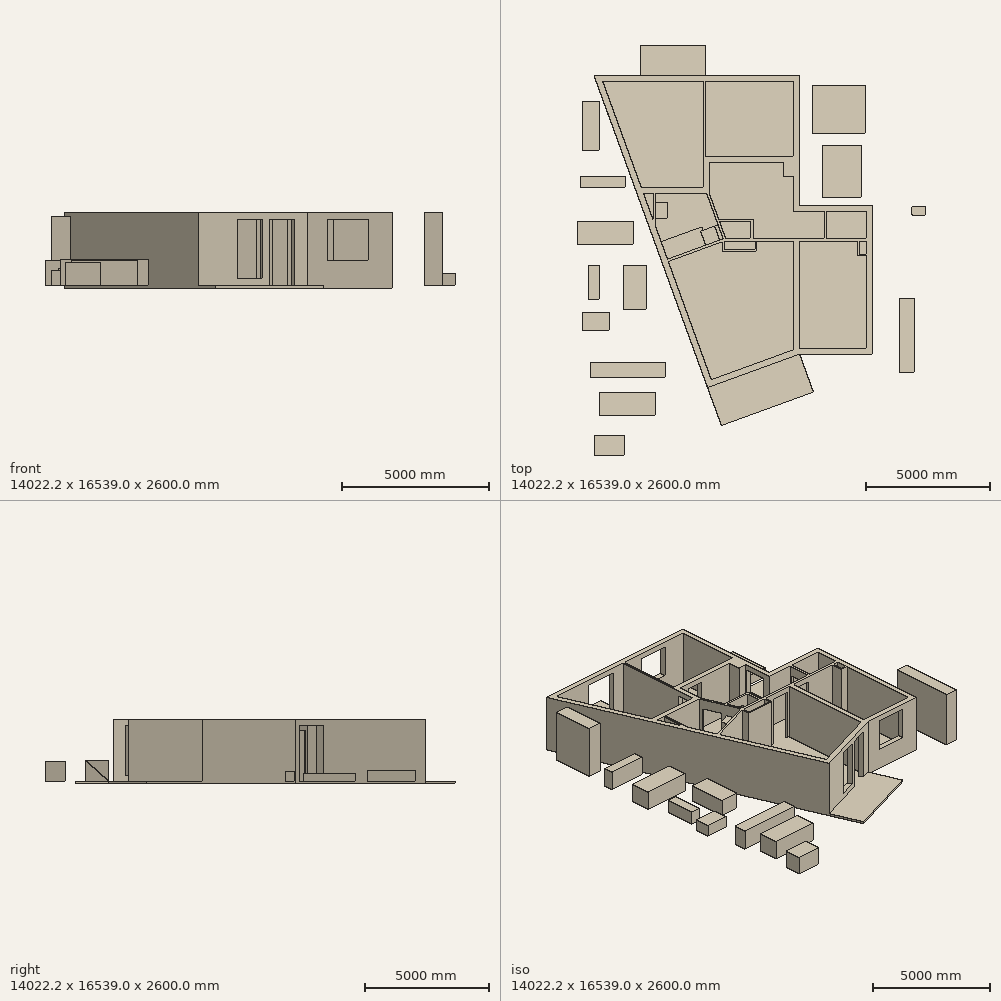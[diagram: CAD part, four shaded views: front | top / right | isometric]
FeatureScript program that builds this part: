
annotation { "Feature Type Name" : "Feature", "Feature Type Description" : "" }
export const myFeature = defineFeature(function(context is Context, id is Id, definition is map)
    precondition{}
    {
        {
            var Q0;
            Q0=qCreatedBy(makeId("Top.planeOp"),FACE);
            var sketch = newSketch(context, id + "F0", { "sketchPlane" : qUnion([Q0])});
            skLineSegment(sketch, "E0", {"start": v(0, 0) * mm, "end": v(8300, 0) * mm});
            skLineSegment(sketch, "E1", {"start": v(8300, 0) * mm, "end": v(8300, -5250) * mm});
            skLineSegment(sketch, "E2", {"start": v(8300, -11255.04) * mm, "end": v(4588.21, -12606.01) * mm});
            skLineSegment(sketch, "E3", {"start": v(4588.21, -12606.01) * mm, "end": v(0, 0) * mm});
            skLineSegment(sketch, "E4.0", {"start": v(357.04, -250) * mm, "end": v(4402.04, -250) * mm});
            skLineSegment(sketch, "E4.1", {"start": v(4737.63, -12285.59) * mm, "end": v(3002.37, -7518) * mm});
            skLineSegment(sketch, "E4.2", {"start": v(8050, -11079.98) * mm, "end": v(4737.63, -12285.59) * mm});
            skLineSegment(sketch, "E4.3", {"start": v(8050, -250) * mm, "end": v(8050, -3260) * mm});
            skLineSegment(sketch, "E5", {"start": v(8050, -3260) * mm, "end": v(4502.04, -3260) * mm});
            skLineSegment(sketch, "E6", {"start": v(4402.04, -3260) * mm, "end": v(4402.04, -4510) * mm});
            skLineSegment(sketch, "E7", {"start": v(4402.04, -4510) * mm, "end": v(1907.55, -4510) * mm});
            skLineSegment(sketch, "E8.0", {"start": v(4545.62, -4760) * mm, "end": v(2498.54, -4760) * mm});
            skLineSegment(sketch, "E8.1", {"start": v(4652.04, -3510) * mm, "end": v(4652.04, -4760) * mm});
            skLineSegment(sketch, "E8.2", {"start": v(8050, -3510) * mm, "end": v(4652.04, -3510) * mm});
            skLineSegment(sketch, "E9", {"start": v(4402.04, -3260) * mm, "end": v(4402.04, -250) * mm});
            skLineSegment(sketch, "E10.0", {"start": v(4502.04, -3260) * mm, "end": v(4502.04, -250) * mm});
            skLineSegment(sketch, "E11", {"start": v(3002.37, -7518) * mm, "end": v(5192.37, -6720.9) * mm});
            skLineSegment(sketch, "E12", {"start": v(4652.04, -4760) * mm, "end": v(5032.4, -5805.04) * mm});
            skLineSegment(sketch, "E13.0", {"start": v(4545.62, -4760) * mm, "end": v(5217.3, -6605.41) * mm});
            skLineSegment(sketch, "E13.1", {"start": v(2968.17, -7424.03) * mm, "end": v(5217.3, -6605.41) * mm});
            skLineSegment(sketch, "E14", {"start": v(2498.54, -4760) * mm, "end": v(2498.54, -6133.74) * mm});
            skLineSegment(sketch, "E15.0", {"start": v(2398.54, -4760) * mm, "end": v(2398.54, -5859) * mm});
            skLineSegment(sketch, "E16", {"start": v(4588.21, -12606.01) * mm, "end": v(5145.7, -14137.71) * mm});
            skLineSegment(sketch, "E17", {"start": v(5145.7, -14137.71) * mm, "end": v(8857.5, -12786.73) * mm});
            skLineSegment(sketch, "E18", {"start": v(8857.5, -12786.73) * mm, "end": v(8300, -11255.04) * mm});
            skLineSegment(sketch, "E19", {"start": v(8300, -5250) * mm, "end": v(11220, -5250) * mm});
            skLineSegment(sketch, "E20", {"start": v(11220, -5250) * mm, "end": v(11220, -11255.04) * mm});
            skLineSegment(sketch, "E21", {"start": v(11220, -11255.04) * mm, "end": v(8300, -11255.04) * mm});
            skLineSegment(sketch, "E22.0", {"start": v(8300, -5500) * mm, "end": v(9300, -5500) * mm});
            skLineSegment(sketch, "E23.0", {"start": v(11000, -5500) * mm, "end": v(11000, -6605.04) * mm});
            skLineSegment(sketch, "E24.0", {"start": v(11000, -11005.04) * mm, "end": v(8300, -11005.04) * mm});
            skLineSegment(sketch, "E25", {"start": v(1900, 0) * mm, "end": v(1900, 1200) * mm});
            skLineSegment(sketch, "E26", {"start": v(1900, 1200) * mm, "end": v(4500, 1200) * mm});
            skLineSegment(sketch, "E27", {"start": v(4500, 1200) * mm, "end": v(4500, 0) * mm});
            skLineSegment(sketch, "E28", {"start": v(11000, -6605.04) * mm, "end": v(9400, -6605.04) * mm});
            skLineSegment(sketch, "E29.0", {"start": v(11000, -6705.04) * mm, "end": v(10710, -6705.04) * mm});
            skLineSegment(sketch, "E30", {"start": v(6323.57, -6605.04) * mm, "end": v(6323.57, -5905.04) * mm});
            skLineSegment(sketch, "E31", {"start": v(6323.57, -5905.04) * mm, "end": v(5068.8, -5905.04) * mm});
            skLineSegment(sketch, "E32.0", {"start": v(6423.57, -5805.04) * mm, "end": v(5032.4, -5805.04) * mm});
            skLineSegment(sketch, "E32.1", {"start": v(6423.57, -6605.04) * mm, "end": v(6423.57, -5805.04) * mm});
            skLineSegment(sketch, "E33", {"start": v(9400, -6605.04) * mm, "end": v(9400, -5500) * mm});
            skLineSegment(sketch, "E34.0", {"start": v(9300, -6605.04) * mm, "end": v(9300, -5500) * mm});
            skLineSegment(sketch, "E35", {"start": v(6512.37, -6705.04) * mm, "end": v(6512.37, -7045.04) * mm});
            skLineSegment(sketch, "E36", {"start": v(6512.37, -7045.04) * mm, "end": v(5252.37, -7045.04) * mm});
            skLineSegment(sketch, "E37", {"start": v(5252.37, -7045.04) * mm, "end": v(5252.37, -6705.04) * mm});
            skLineSegment(sketch, "E38.0", {"start": v(5192.37, -7105.04) * mm, "end": v(5192.37, -6720.9) * mm});
            skLineSegment(sketch, "E38.1", {"start": v(6572.37, -7105.04) * mm, "end": v(5192.37, -7105.04) * mm});
            skLineSegment(sketch, "E38.2", {"start": v(6572.37, -6705.04) * mm, "end": v(6572.37, -7105.04) * mm});
            skLineSegment(sketch, "E39", {"start": v(10650, -6705.04) * mm, "end": v(10650, -7275.04) * mm});
            skLineSegment(sketch, "E40", {"start": v(10650, -7275.04) * mm, "end": v(11000, -7275.04) * mm});
            skLineSegment(sketch, "E41.0", {"start": v(10710, -7215.04) * mm, "end": v(11000, -7215.04) * mm});
            skLineSegment(sketch, "E41.1", {"start": v(10710, -6705.04) * mm, "end": v(10710, -7215.04) * mm});
            skLineSegment(sketch, "E42.trimOffspring", {"start": v(4502.04, -250) * mm, "end": v(8050, -250) * mm});
            skLineSegment(sketch, "E43.trimOffspring", {"start": v(1907.55, -4510) * mm, "end": v(357.04, -250) * mm});
            skLineSegment(sketch, "E44.trimOffspring", {"start": v(2398.54, -5859) * mm, "end": v(1998.54, -4760) * mm});
            skLineSegment(sketch, "E45.trimOffspring", {"start": v(2398.54, -4760) * mm, "end": v(1998.54, -4760) * mm});
            skLineSegment(sketch, "E46.trimOffspring", {"start": v(2968.17, -7424.03) * mm, "end": v(2498.54, -6133.74) * mm});
            skLineSegment(sketch, "E47.trimOffspring", {"start": v(5068.8, -5905.04) * mm, "end": v(5323.57, -6605.04) * mm});
            skLineSegment(sketch, "E48.trimOffspring", {"start": v(6323.57, -6605.04) * mm, "end": v(5323.57, -6605.04) * mm});
            skLineSegment(sketch, "E49.trimOffspring", {"start": v(6512.37, -6705.04) * mm, "end": v(5252.37, -6705.04) * mm});
            skLineSegment(sketch, "E50.trimOffspring", {"start": v(8050, -6705.04) * mm, "end": v(6572.37, -6705.04) * mm});
            skLineSegment(sketch, "E51.trimOffspring", {"start": v(8050, -6705.04) * mm, "end": v(8050, -11079.98) * mm});
            skLineSegment(sketch, "E52.trimOffspring", {"start": v(8050, -6605.04) * mm, "end": v(6423.57, -6605.04) * mm});
            skLineSegment(sketch, "E53.trimOffspring", {"start": v(8300, -5500) * mm, "end": v(8300, -6605.04) * mm});
            skLineSegment(sketch, "E54.trimOffspring", {"start": v(8300, -6705.04) * mm, "end": v(8300, -11005.04) * mm});
            skLineSegment(sketch, "E55.trimOffspring", {"start": v(9300, -6605.04) * mm, "end": v(8300, -6605.04) * mm});
            skLineSegment(sketch, "E56.trimOffspring", {"start": v(9400, -5500) * mm, "end": v(11000, -5500) * mm});
            skLineSegment(sketch, "E57.trimOffspring", {"start": v(10650, -6705.04) * mm, "end": v(8300, -6705.04) * mm});
            skLineSegment(sketch, "E58.trimOffspring", {"start": v(11000, -6705.04) * mm, "end": v(11000, -7215.04) * mm});
            skLineSegment(sketch, "E59.trimOffspring", {"start": v(11000, -7275.04) * mm, "end": v(11000, -11005.04) * mm});
            skLineSegment(sketch, "E60.trimOffspring", {"start": v(8050, -3510) * mm, "end": v(8050, -6605.04) * mm});
            skSolve(sketch);
        }
        {
            var Q0;
            Q0=makeQuery(id+"F0.imprint","IMPRINT",FACE,{"disambiguationData":[TD([[makeQuery(id+"F0.imprint","IMPRINT",EDGE,{"derivedFrom":sQuery(id+"F0.wireOp",EDGE,"E8.1")}),1.0]])]});
            var Q1;
            Q1=makeQuery(id+"F0.imprint","IMPRINT",FACE,{"disambiguationData":[TD([[makeQuery(id+"F0.imprint","IMPRINT",EDGE,{"derivedFrom":sQuery(id+"F0.wireOp",EDGE,"E30")}),1.0]])]});
            var Q2;
            {var subQ2=sQuery(id+"F0.wireOp",EDGE,"E5");Q2=makeQuery(id+"F0.imprint","IMPRINT",FACE,{"disambiguationData":[TD([[makeQuery(id+"F0.imprint","IMPRINT",EDGE,{"derivedFrom":subQ2}),-1.0]])]});}
            var Q3;
            Q3=makeQuery(id+"F0.imprint","IMPRINT",FACE,{"disambiguationData":[TD([[makeQuery(id+"F0.imprint","IMPRINT",EDGE,{"derivedFrom":sQuery(id+"F0.wireOp",EDGE,"E8.0")}),1.0]])]});
            var Q4;
            Q4=makeQuery(id+"F0.imprint","IMPRINT",FACE,{"disambiguationData":[TD([[makeQuery(id+"F0.imprint","IMPRINT",EDGE,{"derivedFrom":sQuery(id+"F0.wireOp",EDGE,"E24.0")}),-1.0]])]});
            var Q5;
            Q5=makeQuery(id+"F0.imprint","IMPRINT",FACE,{"disambiguationData":[TD([[makeQuery(id+"F0.imprint","IMPRINT",EDGE,{"derivedFrom":sQuery(id+"F0.wireOp",EDGE,"E23.0")}),-1.0]])]});
            var Q6;
            Q6=makeQuery(id+"F0.imprint","IMPRINT",FACE,{"disambiguationData":[TD([[makeQuery(id+"F0.imprint","IMPRINT",EDGE,{"derivedFrom":sQuery(id+"F0.wireOp",EDGE,"E4.0")}),-1.0]])]});
            var Q7;
            Q7=makeQuery(id+"F0.imprint","IMPRINT",FACE,{"disambiguationData":[TD([[makeQuery(id+"F0.imprint","IMPRINT",EDGE,{"derivedFrom":sQuery(id+"F0.wireOp",EDGE,"E22.0")}),-1.0]])]});
            var Q8;
            Q8=makeQuery(id+"F0.imprint","IMPRINT",FACE,{"disambiguationData":[TD([[makeQuery(id+"F0.imprint","IMPRINT",EDGE,{"derivedFrom":sQuery(id+"F0.wireOp",EDGE,"E4.1")}),-1.0]])]});
            var Q9;
            Q9=makeQuery(id+"F0.imprint","IMPRINT",FACE,{"disambiguationData":[TD([[makeQuery(id+"F0.imprint","IMPRINT",EDGE,{"derivedFrom":sQuery(id+"F0.wireOp",EDGE,"E2")}),1.0]])]});
            var Q10;
            {var subQ0=sQuery(id+"F0.wireOp",EDGE,"E25");Q10=makeQuery(id+"F0.imprint","IMPRINT",FACE,{"disambiguationData":[TD([[makeQuery(id+"F0.imprint","IMPRINT",EDGE,{"derivedFrom":subQ0}),-1.0]])]});}
            var Q11;
            {var subQ7=sQuery(id+"F0.wireOp",EDGE,"E1");Q11=makeQuery(id+"F0.imprint","IMPRINT",FACE,{"disambiguationData":[TD([[makeQuery(id+"F0.imprint","IMPRINT",EDGE,{"derivedFrom":subQ7}),-1.0]])]});}
            var Q12;
            Q12=makeQuery(id+"F0.imprint","IMPRINT",FACE,{"disambiguationData":[TD([[makeQuery(id+"F0.imprint","IMPRINT",EDGE,{"derivedFrom":sQuery(id+"F0.wireOp",EDGE,"E35")}),-1.0]])]});
            var Q13;
            Q13=makeQuery(id+"F0.imprint","IMPRINT",FACE,{"disambiguationData":[TD([[makeQuery(id+"F0.imprint","IMPRINT",EDGE,{"derivedFrom":sQuery(id+"F0.wireOp",EDGE,"E15.0")}),-1.0]])]});
            var Q14;
            Q14=makeQuery(id+"F0.imprint","IMPRINT",FACE,{"disambiguationData":[TD([[makeQuery(id+"F0.imprint","IMPRINT",EDGE,{"derivedFrom":sQuery(id+"F0.wireOp",EDGE,"E29.0")}),1.0]])]});
            extrude(context, id + "F1", {"entities" : qUnion([Q0, Q1, Q2, Q3, Q4, Q5, Q6, Q7, Q8, Q9, Q10, Q11, Q12, Q13, Q14]), "oppositeDirection" : true, "depth" : 100 * mm});
        }
        {
            var Q0;
            {var subQ4=sQuery(id+"F0.wireOp",EDGE,"E1");Q0=makeQuery(id+"F0.imprint","IMPRINT",FACE,{"disambiguationData":[TD([[makeQuery(id+"F0.imprint","IMPRINT",EDGE,{"derivedFrom":subQ4}),-1.0]])]});}
            extrude(context, id + "F2", {"entities" : qUnion([Q0]), "operationType" : NewBodyOperationType.ADD, "depth" : 2500 * mm});
        }
        {
            var Q0;
            Q0=makeQuery(id+"F2.opExtrude","SWEPT_FACE",FACE,{"disambiguationData":[OSD([sQuery(id+"F0.wireOp",EDGE,"E4.2")])]});
            var sketch = newSketch(context, id + "F3", { "sketchPlane" : qUnion([Q0])});
            skLineSegment(sketch, "E61.bottom", {"start": v(-3475, 0) * mm, "end": v(-2575, 0) * mm});
            skLineSegment(sketch, "E61.top", {"start": v(-3475, 2250) * mm, "end": v(-2575, 2250) * mm});
            skLineSegment(sketch, "E61.left", {"start": v(-3475, 0) * mm, "end": v(-3475, 2250) * mm});
            skLineSegment(sketch, "E61.right", {"start": v(-2575, 0) * mm, "end": v(-2575, 2250) * mm});
            skLineSegment(sketch, "E62.bottom", {"start": v(-2325, 2250) * mm, "end": v(-1425, 2250) * mm});
            skLineSegment(sketch, "E62.top", {"start": v(-2325, 250) * mm, "end": v(-1425, 250) * mm});
            skLineSegment(sketch, "E62.left", {"start": v(-2325, 2250) * mm, "end": v(-2325, 250) * mm});
            skLineSegment(sketch, "E62.right", {"start": v(-1425, 2250) * mm, "end": v(-1425, 250) * mm});
            skSolve(sketch);
        }
        {
            var Q0;
            Q0=makeQuery(id+"F3.imprint","IMPRINT",FACE,{"disambiguationData":[TD([[makeQuery(id+"F3.imprint","IMPRINT",EDGE,{"derivedFrom":sQuery(id+"F3.wireOp",EDGE,"E62.bottom")}),-1.0]])]});
            var Q1;
            Q1=makeQuery(id+"F3.imprint","IMPRINT",FACE,{"disambiguationData":[TD([[makeQuery(id+"F3.imprint","IMPRINT",EDGE,{"derivedFrom":sQuery(id+"F3.wireOp",EDGE,"E61.bottom")}),1.0]])]});
            extrude(context, id + "F4", {"entities" : qUnion([Q0, Q1]), "operationType" : NewBodyOperationType.REMOVE, "endBound" : BoundingType.THROUGH_ALL, "oppositeDirection" : true, "depth" : 25 * mm});
        }
        {
            var Q0;
            Q0=makeQuery(id+"F2.opExtrude","SWEPT_FACE",FACE,{"disambiguationData":[OSD([sQuery(id+"F0.wireOp",EDGE,"E4.0")])]});
            var sketch = newSketch(context, id + "F5", { "sketchPlane" : qUnion([Q0])});
            skLineSegment(sketch, "E63.bottom", {"start": v(3800, 0) * mm, "end": v(2900, 0) * mm});
            skLineSegment(sketch, "E63.top", {"start": v(3800, 2250) * mm, "end": v(2900, 2250) * mm});
            skLineSegment(sketch, "E63.left", {"start": v(3800, 0) * mm, "end": v(3800, 2250) * mm});
            skLineSegment(sketch, "E63.right", {"start": v(2900, 0) * mm, "end": v(2900, 2250) * mm});
            skLineSegment(sketch, "E64.bottom", {"start": v(2900, 2250) * mm, "end": v(2300, 2250) * mm});
            skLineSegment(sketch, "E64.top", {"start": v(2900, 850) * mm, "end": v(2300, 850) * mm});
            skLineSegment(sketch, "E64.left", {"start": v(2900, 2250) * mm, "end": v(2900, 850) * mm});
            skLineSegment(sketch, "E64.right", {"start": v(2300, 2250) * mm, "end": v(2300, 850) * mm});
            skLineSegment(sketch, "E65.0", {"start": v(0, -100) * mm, "end": v(0, 2500) * mm});
            skSolve(sketch);
        }
        {
            var Q0;
            Q0=makeQuery(id+"F5.imprint","IMPRINT",FACE,{"disambiguationData":[TD([[makeQuery(id+"F5.imprint","IMPRINT",EDGE,{"derivedFrom":sQuery(id+"F5.wireOp",EDGE,"E64.bottom")}),1.0]])]});
            var Q1;
            Q1=makeQuery(id+"F5.imprint","IMPRINT",FACE,{"disambiguationData":[TD([[makeQuery(id+"F5.imprint","IMPRINT",EDGE,{"derivedFrom":sQuery(id+"F5.wireOp",EDGE,"E63.bottom")}),1.0]])]});
            extrude(context, id + "F6", {"entities" : qUnion([Q0, Q1]), "operationType" : NewBodyOperationType.REMOVE, "endBound" : BoundingType.THROUGH_ALL, "oppositeDirection" : true, "depth" : 25 * mm});
        }
        {
            var Q0;
            Q0=makeQuery(id+"F2.opExtrude","SWEPT_FACE",FACE,{"disambiguationData":[OSD([sQuery(id+"F0.wireOp",EDGE,"E42.trimOffspring")])]});
            var sketch = newSketch(context, id + "F7", { "sketchPlane" : qUnion([Q0])});
            skLineSegment(sketch, "E66.bottom", {"start": v(5550, 2250) * mm, "end": v(6950, 2250) * mm});
            skLineSegment(sketch, "E66.top", {"start": v(5550, 850) * mm, "end": v(6950, 850) * mm});
            skLineSegment(sketch, "E66.left", {"start": v(5550, 2250) * mm, "end": v(5550, 850) * mm});
            skLineSegment(sketch, "E66.right", {"start": v(6950, 2250) * mm, "end": v(6950, 850) * mm});
            skLineSegment(sketch, "E67.0", {"start": v(0, -100) * mm, "end": v(0, 2500) * mm});
            skSolve(sketch);
        }
        {
            var Q0;
            Q0=makeQuery(id+"F7.imprint","IMPRINT",FACE,{"disambiguationData":[TD([[makeQuery(id+"F7.imprint","IMPRINT",EDGE,{"derivedFrom":sQuery(id+"F7.wireOp",EDGE,"E66.bottom")}),-1.0]])]});
            extrude(context, id + "F8", {"entities" : qUnion([Q0]), "operationType" : NewBodyOperationType.REMOVE, "endBound" : BoundingType.THROUGH_ALL, "oppositeDirection" : true, "depth" : 25 * mm});
        }
        {
            var Q0;
            Q0=makeQuery(id+"F2.opExtrude","SWEPT_FACE",FACE,{"disambiguationData":[OSD([sQuery(id+"F0.wireOp",EDGE,"E24.0")])]});
            var sketch = newSketch(context, id + "F9", { "sketchPlane" : qUnion([Q0])});
            skLineSegment(sketch, "E68.bottom", {"start": v(-10400, 850) * mm, "end": v(-9000, 850) * mm});
            skLineSegment(sketch, "E68.top", {"start": v(-10400, 2250) * mm, "end": v(-9000, 2250) * mm});
            skLineSegment(sketch, "E68.left", {"start": v(-10400, 850) * mm, "end": v(-10400, 2250) * mm});
            skLineSegment(sketch, "E68.right", {"start": v(-9000, 850) * mm, "end": v(-9000, 2250) * mm});
            skSolve(sketch);
        }
        {
            var Q0;
            Q0=makeQuery(id+"F9.imprint","IMPRINT",FACE,{"disambiguationData":[TD([[makeQuery(id+"F9.imprint","IMPRINT",EDGE,{"derivedFrom":sQuery(id+"F9.wireOp",EDGE,"E68.bottom")}),1.0]])]});
            extrude(context, id + "F10", {"entities" : qUnion([Q0]), "operationType" : NewBodyOperationType.REMOVE, "endBound" : BoundingType.THROUGH_ALL, "oppositeDirection" : true, "depth" : 25 * mm});
        }
        {
            var Q0;
            Q0=makeQuery(id+"F2.opExtrude","SWEPT_FACE",FACE,{"disambiguationData":[OSD([sQuery(id+"F0.wireOp",EDGE,"E34.0")])]});
            var sketch = newSketch(context, id + "F11", { "sketchPlane" : qUnion([Q0])});
            skLineSegment(sketch, "E69", {"start": v(6052.52, 0) * mm, "end": v(6502.52, 0) * mm});
            skLineSegment(sketch, "E70", {"start": v(6502.52, 0) * mm, "end": v(6502.52, 2050) * mm});
            skLineSegment(sketch, "E71", {"start": v(6502.52, 2050) * mm, "end": v(5602.52, 2050) * mm});
            skLineSegment(sketch, "E72", {"start": v(5602.52, 2050) * mm, "end": v(5602.52, 0) * mm});
            skLineSegment(sketch, "E73", {"start": v(5602.52, 0) * mm, "end": v(6052.52, 0) * mm});
            skSolve(sketch);
        }
        {
            var Q0;
            Q0=makeQuery(id+"F11.imprint","IMPRINT",FACE,{"disambiguationData":[TD([[makeQuery(id+"F11.imprint","IMPRINT",EDGE,{"derivedFrom":sQuery(id+"F11.wireOp",EDGE,"E69")}),-1.0]])]});
            extrude(context, id + "F12", {"entities" : qUnion([Q0]), "operationType" : NewBodyOperationType.REMOVE, "endBound" : BoundingType.UP_TO_NEXT, "oppositeDirection" : true, "depth" : 25 * mm});
        }
        {
            var Q0;
            Q0=makeQuery(id+"F2.opExtrude","SWEPT_FACE",FACE,{"disambiguationData":[OSD([sQuery(id+"F0.wireOp",EDGE,"E55.trimOffspring")])]});
            var sketch = newSketch(context, id + "F13", { "sketchPlane" : qUnion([Q0])});
            skLineSegment(sketch, "E74", {"start": v(-8800, 0) * mm, "end": v(-8400, 0) * mm});
            skLineSegment(sketch, "E75", {"start": v(-8400, 0) * mm, "end": v(-8400, 2250) * mm});
            skLineSegment(sketch, "E76", {"start": v(-8400, 2250) * mm, "end": v(-9200, 2250) * mm});
            skLineSegment(sketch, "E77", {"start": v(-9200, 2250) * mm, "end": v(-9200, 0) * mm});
            skLineSegment(sketch, "E78", {"start": v(-9200, 0) * mm, "end": v(-8800, 0) * mm});
            skSolve(sketch);
        }
        {
            var Q0;
            Q0=makeQuery(id+"F13.imprint","IMPRINT",FACE,{"disambiguationData":[TD([[makeQuery(id+"F13.imprint","IMPRINT",EDGE,{"derivedFrom":sQuery(id+"F13.wireOp",EDGE,"E74")}),1.0]])]});
            extrude(context, id + "F14", {"entities" : qUnion([Q0]), "operationType" : NewBodyOperationType.REMOVE, "endBound" : BoundingType.UP_TO_NEXT, "oppositeDirection" : true, "depth" : 25 * mm});
        }
        {
            var Q0;
            Q0=makeQuery(id+"F2.opExtrude","SWEPT_FACE",FACE,{"disambiguationData":[OSD([sQuery(id+"F0.wireOp",EDGE,"E53.trimOffspring")])]});
            var sketch = newSketch(context, id + "F15", { "sketchPlane" : qUnion([Q0])});
            skLineSegment(sketch, "E79.bottom", {"start": v(-6605.04, 0) * mm, "end": v(-5500, 0) * mm});
            skLineSegment(sketch, "E79.top", {"start": v(-6605.04, 2500) * mm, "end": v(-5500, 2500) * mm});
            skLineSegment(sketch, "E79.left", {"start": v(-6605.04, 0) * mm, "end": v(-6605.04, 2500) * mm});
            skLineSegment(sketch, "E79.right", {"start": v(-5500, 0) * mm, "end": v(-5500, 2500) * mm});
            skSolve(sketch);
        }
        {
            var Q0;
            Q0 = qSketchRegion(id + "F15", true);
            extrude(context, id + "F16", {"entities" : qUnion([Q0]), "operationType" : NewBodyOperationType.REMOVE, "endBound" : BoundingType.UP_TO_NEXT, "oppositeDirection" : true, "depth" : 25 * mm});
        }
        {
            var Q0;
            Q0=makeQuery(id+"F2.opExtrude","SWEPT_FACE",FACE,{"disambiguationData":[OSD([sQuery(id+"F0.wireOp",EDGE,"E31")])]});
            var sketch = newSketch(context, id + "F17", { "sketchPlane" : qUnion([Q0])});
            skLineSegment(sketch, "E80", {"start": v(5696.19, 0) * mm, "end": v(6046.19, 0) * mm});
            skLineSegment(sketch, "E81", {"start": v(6046.19, 0) * mm, "end": v(6046.19, 2050) * mm});
            skLineSegment(sketch, "E82", {"start": v(6046.19, 2050) * mm, "end": v(5346.19, 2050) * mm});
            skLineSegment(sketch, "E83", {"start": v(5346.19, 2050) * mm, "end": v(5346.19, 0) * mm});
            skLineSegment(sketch, "E84", {"start": v(5346.19, 0) * mm, "end": v(5696.19, 0) * mm});
            skSolve(sketch);
        }
        {
            var Q0;
            Q0 = qSketchRegion(id + "F17", true);
            extrude(context, id + "F18", {"entities" : qUnion([Q0]), "operationType" : NewBodyOperationType.REMOVE, "endBound" : BoundingType.UP_TO_NEXT, "oppositeDirection" : true, "depth" : 25 * mm});
        }
        {
            var Q0;
            Q0=makeQuery(id+"F2.opExtrude","SWEPT_FACE",FACE,{"disambiguationData":[OSD([sQuery(id+"F0.wireOp",EDGE,"E60.trimOffspring")])]});
            var sketch = newSketch(context, id + "F19", { "sketchPlane" : qUnion([Q0])});
            skLineSegment(sketch, "E85.bottom", {"start": v(5110, 0) * mm, "end": v(4110, 0) * mm});
            skLineSegment(sketch, "E85.top", {"start": v(5110, 2250) * mm, "end": v(4110, 2250) * mm});
            skLineSegment(sketch, "E85.left", {"start": v(5110, 0) * mm, "end": v(5110, 2250) * mm});
            skLineSegment(sketch, "E85.right", {"start": v(4110, 0) * mm, "end": v(4110, 2250) * mm});
            skSolve(sketch);
        }
        {
            var Q0;
            Q0 = qSketchRegion(id + "F19", true);
            extrude(context, id + "F20", {"entities" : qUnion([Q0]), "operationType" : NewBodyOperationType.REMOVE, "endBound" : BoundingType.UP_TO_NEXT, "oppositeDirection" : true, "depth" : 25 * mm});
        }
        {
            var Q0;
            Q0=makeQuery(id+"F2.opExtrude","SWEPT_FACE",FACE,{"disambiguationData":[OSD([sQuery(id+"F0.wireOp",EDGE,"E8.2")])]});
            var sketch = newSketch(context, id + "F21", { "sketchPlane" : qUnion([Q0])});
            skLineSegment(sketch, "E86.bottom", {"start": v(5132.04, 0) * mm, "end": v(5932.04, 0) * mm});
            skLineSegment(sketch, "E86.top", {"start": v(5132.04, 2250) * mm, "end": v(5932.04, 2250) * mm});
            skLineSegment(sketch, "E86.left", {"start": v(5132.04, 0) * mm, "end": v(5132.04, 2250) * mm});
            skLineSegment(sketch, "E86.right", {"start": v(5932.04, 0) * mm, "end": v(5932.04, 2250) * mm});
            skSolve(sketch);
        }
        {
            var Q0;
            Q0 = qSketchRegion(id + "F21", true);
            extrude(context, id + "F22", {"entities" : qUnion([Q0]), "operationType" : NewBodyOperationType.REMOVE, "endBound" : BoundingType.UP_TO_NEXT, "oppositeDirection" : true, "depth" : 25 * mm});
        }
        {
            var Q0;
            Q0=makeQuery(id+"F2.opExtrude","SWEPT_FACE",FACE,{"disambiguationData":[OSD([sQuery(id+"F0.wireOp",EDGE,"E8.1")])]});
            var sketch = newSketch(context, id + "F23", { "sketchPlane" : qUnion([Q0])});
            skLineSegment(sketch, "E87.0", {"start": v(-4510, 2500) * mm, "end": v(-4510, 0) * mm});
            skLineSegment(sketch, "E88.bottom", {"start": v(-4410, 0) * mm, "end": v(-3610, 0) * mm});
            skLineSegment(sketch, "E88.top", {"start": v(-4410, 2250) * mm, "end": v(-3610, 2250) * mm});
            skLineSegment(sketch, "E88.left", {"start": v(-4410, 0) * mm, "end": v(-4410, 2250) * mm});
            skLineSegment(sketch, "E88.right", {"start": v(-3610, 0) * mm, "end": v(-3610, 2250) * mm});
            skSolve(sketch);
        }
        {
            var Q0;
            Q0 = qSketchRegion(id + "F23", true);
            extrude(context, id + "F24", {"entities" : qUnion([Q0]), "operationType" : NewBodyOperationType.REMOVE, "endBound" : BoundingType.UP_TO_NEXT, "oppositeDirection" : true, "depth" : 25 * mm});
        }
        {
            var Q0;
            Q0=makeQuery(id+"F2.opExtrude","SWEPT_FACE",FACE,{"disambiguationData":[OSD([sQuery(id+"F0.wireOp",EDGE,"E50.trimOffspring")])]});
            var sketch = newSketch(context, id + "F25", { "sketchPlane" : qUnion([Q0])});
            skLineSegment(sketch, "E89.bottom", {"start": v(7910, 0) * mm, "end": v(7110, 0) * mm});
            skLineSegment(sketch, "E89.top", {"start": v(7910, 2250) * mm, "end": v(7110, 2250) * mm});
            skLineSegment(sketch, "E89.left", {"start": v(7910, 0) * mm, "end": v(7910, 2250) * mm});
            skLineSegment(sketch, "E89.right", {"start": v(7110, 0) * mm, "end": v(7110, 2250) * mm});
            skSolve(sketch);
        }
        {
            var Q0;
            Q0 = qSketchRegion(id + "F25", true);
            extrude(context, id + "F26", {"entities" : qUnion([Q0]), "operationType" : NewBodyOperationType.REMOVE, "endBound" : BoundingType.UP_TO_NEXT, "oppositeDirection" : true, "depth" : 25 * mm});
        }
        {
            var Q0;
            Q0=makeQuery(id+"F2.opExtrude","SWEPT_FACE",FACE,{"disambiguationData":[OSD([sQuery(id+"F0.wireOp",EDGE,"E12")])]});
            var sketch = newSketch(context, id + "F27", { "sketchPlane" : qUnion([Q0])});
            skLineSegment(sketch, "E90", {"start": v(-6620.08, 0) * mm, "end": v(-6170.08, 0) * mm});
            skLineSegment(sketch, "E91", {"start": v(-6170.08, 0) * mm, "end": v(-6170.08, 2050) * mm});
            skLineSegment(sketch, "E92", {"start": v(-6170.08, 2050) * mm, "end": v(-7070.08, 2050) * mm});
            skLineSegment(sketch, "E93", {"start": v(-7070.08, 2050) * mm, "end": v(-7070.08, 0) * mm});
            skLineSegment(sketch, "E94", {"start": v(-7070.08, 0) * mm, "end": v(-6620.08, 0) * mm});
            skSolve(sketch);
        }
        {
            var Q0;
            Q0 = qSketchRegion(id + "F27", true);
            extrude(context, id + "F28", {"entities" : qUnion([Q0]), "operationType" : NewBodyOperationType.REMOVE, "endBound" : BoundingType.UP_TO_NEXT, "oppositeDirection" : true, "depth" : 25 * mm});
        }
        {
            var Q0;
            {var subQ0=sQuery(id+"F0.wireOp",EDGE,"E27");var subQ1=sQuery(id+"F0.wireOp",EDGE,"E26");var subQ2=sQuery(id+"F0.wireOp",EDGE,"E25");var subQ3=sQuery(id+"F0.wireOp",EDGE,"E21");var subQ4=sQuery(id+"F0.wireOp",EDGE,"E18");var subQ5=sQuery(id+"F0.wireOp",EDGE,"E17");var subQ6=sQuery(id+"F0.wireOp",EDGE,"E16");var subQ7=sQuery(id+"F0.wireOp",EDGE,"E3");var subQ8=sQuery(id+"F0.wireOp",EDGE,"E1");var subQ9=sQuery(id+"F0.wireOp",EDGE,"E0");var subQ10=makeQuery(id+"F1.opExtrude","CAP_FACE",FACE,{"disambiguationData":[OSD([subQ9,subQ8,subQ7,subQ6,subQ5,subQ4,sQuery(id+"F0.wireOp",EDGE,"E19"),sQuery(id+"F0.wireOp",EDGE,"E20"),subQ3,subQ2,subQ1,subQ0])],"isStart":true});Q0=makeQuery(id+"F28.boolean.opBoolean","MERGE",FACE,{"derivedFrom":[makeQuery(id+"F2.boolean.opBoolean","SPLIT",FACE,{"disambiguationData":[TD([makeQuery(id+"F2.opExtrude","SWEPT_FACE",FACE,{"disambiguationData":[OSD([sQuery(id+"F0.wireOp",EDGE,"E8.0")])]})])],"derivedFrom":subQ10}),makeQuery(id+"F26.boolean.opBoolean","MERGE",FACE,{"derivedFrom":[makeQuery(id+"F4.boolean.opBoolean","MERGE",FACE,{"derivedFrom":[makeQuery(id+"F2.boolean.opBoolean","SPLIT",FACE,{"disambiguationData":[TD([makeQuery(id+"F1.opExtrude","SWEPT_FACE",FACE,{"disambiguationData":[OSD([subQ5])]})])],"derivedFrom":subQ10}),makeQuery(id+"F2.boolean.opBoolean","SPLIT",FACE,{"disambiguationData":[TD([makeQuery(id+"F2.opExtrude","SWEPT_FACE",FACE,{"disambiguationData":[OSD([sQuery(id+"F0.wireOp",EDGE,"E4.1")])]})])],"derivedFrom":subQ10}),makeQuery(id+"F4.opExtrude","SWEPT_FACE",FACE,{"disambiguationData":[OSD([sQuery(id+"F3.wireOp",EDGE,"E61.bottom")])]})]}),makeQuery(id+"F24.boolean.opBoolean","MERGE",FACE,{"derivedFrom":[makeQuery(id+"F6.boolean.opBoolean","MERGE",FACE,{"derivedFrom":[makeQuery(id+"F2.boolean.opBoolean","SPLIT",FACE,{"disambiguationData":[TD([makeQuery(id+"F1.opExtrude","SWEPT_FACE",FACE,{"disambiguationData":[OSD([subQ2])]})])],"derivedFrom":subQ10}),makeQuery(id+"F2.boolean.opBoolean","SPLIT",FACE,{"disambiguationData":[TD([makeQuery(id+"F2.opExtrude","SWEPT_FACE",FACE,{"disambiguationData":[OSD([sQuery(id+"F0.wireOp",EDGE,"E4.0")])]})])],"derivedFrom":subQ10}),makeQuery(id+"F6.opExtrude","SWEPT_FACE",FACE,{"disambiguationData":[OSD([sQuery(id+"F5.wireOp",EDGE,"E63.bottom")])]})]}),makeQuery(id+"F22.boolean.opBoolean","MERGE",FACE,{"derivedFrom":[makeQuery(id+"F2.boolean.opBoolean","SPLIT",FACE,{"disambiguationData":[TD([makeQuery(id+"F2.opExtrude","SWEPT_FACE",FACE,{"disambiguationData":[OSD([sQuery(id+"F0.wireOp",EDGE,"E4.3")])]})])],"derivedFrom":subQ10}),makeQuery(id+"F20.boolean.opBoolean","MERGE",FACE,{"derivedFrom":[makeQuery(id+"F18.boolean.opBoolean","MERGE",FACE,{"derivedFrom":[makeQuery(id+"F2.boolean.opBoolean","SPLIT",FACE,{"disambiguationData":[TD([makeQuery(id+"F2.opExtrude","SWEPT_FACE",FACE,{"disambiguationData":[OSD([sQuery(id+"F0.wireOp",EDGE,"E30")])]})])],"derivedFrom":subQ10}),makeQuery(id+"F16.boolean.opBoolean","MERGE",FACE,{"derivedFrom":[makeQuery(id+"F2.boolean.opBoolean","SPLIT",FACE,{"disambiguationData":[TD([makeQuery(id+"F2.opExtrude","SWEPT_FACE",FACE,{"disambiguationData":[OSD([sQuery(id+"F0.wireOp",EDGE,"E8.1")])]})])],"derivedFrom":subQ10}),makeQuery(id+"F14.boolean.opBoolean","MERGE",FACE,{"derivedFrom":[makeQuery(id+"F2.boolean.opBoolean","SPLIT",FACE,{"disambiguationData":[TD([makeQuery(id+"F2.opExtrude","SWEPT_FACE",FACE,{"disambiguationData":[OSD([sQuery(id+"F0.wireOp",EDGE,"E24.0")])]})])],"derivedFrom":subQ10}),makeQuery(id+"F12.boolean.opBoolean","MERGE",FACE,{"derivedFrom":[makeQuery(id+"F2.boolean.opBoolean","SPLIT",FACE,{"disambiguationData":[TD([makeQuery(id+"F2.opExtrude","SWEPT_FACE",FACE,{"disambiguationData":[OSD([sQuery(id+"F0.wireOp",EDGE,"E22.0")])]})])],"derivedFrom":subQ10}),makeQuery(id+"F2.boolean.opBoolean","SPLIT",FACE,{"disambiguationData":[TD([makeQuery(id+"F2.opExtrude","SWEPT_FACE",FACE,{"disambiguationData":[OSD([sQuery(id+"F0.wireOp",EDGE,"E23.0")])]})])],"derivedFrom":subQ10}),makeQuery(id+"F12.opExtrude","SWEPT_FACE",FACE,{"disambiguationData":[OSD([sQuery(id+"F11.wireOp",EDGE,"E69"),sQuery(id+"F11.wireOp",EDGE,"E73")])]})]}),makeQuery(id+"F14.opExtrude","SWEPT_FACE",FACE,{"disambiguationData":[OSD([sQuery(id+"F13.wireOp",EDGE,"E74"),sQuery(id+"F13.wireOp",EDGE,"E78")])]})]}),makeQuery(id+"F16.opExtrude","SWEPT_FACE",FACE,{"disambiguationData":[OSD([sQuery(id+"F15.wireOp",EDGE,"E79.bottom")])]})]}),makeQuery(id+"F18.opExtrude","SWEPT_FACE",FACE,{"disambiguationData":[OSD([sQuery(id+"F17.wireOp",EDGE,"E80"),sQuery(id+"F17.wireOp",EDGE,"E84")])]})]}),makeQuery(id+"F20.opExtrude","SWEPT_FACE",FACE,{"disambiguationData":[OSD([sQuery(id+"F19.wireOp",EDGE,"E85.bottom")])]})]}),makeQuery(id+"F22.opExtrude","SWEPT_FACE",FACE,{"disambiguationData":[OSD([sQuery(id+"F21.wireOp",EDGE,"E86.bottom")])]})]}),makeQuery(id+"F24.opExtrude","SWEPT_FACE",FACE,{"disambiguationData":[OSD([sQuery(id+"F23.wireOp",EDGE,"E88.bottom")])]})]}),makeQuery(id+"F26.opExtrude","SWEPT_FACE",FACE,{"disambiguationData":[OSD([sQuery(id+"F25.wireOp",EDGE,"E89.bottom")])]})]}),makeQuery(id+"F28.opExtrude","SWEPT_FACE",FACE,{"disambiguationData":[OSD([sQuery(id+"F27.wireOp",EDGE,"E90"),sQuery(id+"F27.wireOp",EDGE,"E94")])]})]});}
            var sketch = newSketch(context, id + "F29", { "sketchPlane" : qUnion([Q0])});
            skPoint(sketch, "E95.0", {"position": v(3800, -250) * mm});
            skArc(sketch, "E96", {"start": v(2900, -250) * mm, "mid": v(3163.6, -886.4) * mm, "end": v(3800, -1150) * mm});
            skLineSegment(sketch, "E97", {"start": v(3800, -1150) * mm, "end": v(3800, -250) * mm});
            skArc(sketch, "E98", {"start": v(4402.04, -3610) * mm, "mid": v(3836.35, -3844.31) * mm, "end": v(3602.04, -4410) * mm});
            skLineSegment(sketch, "E99", {"start": v(3602.04, -4410) * mm, "end": v(4402.04, -4410) * mm});
            skArc(sketch, "E100", {"start": v(5932.04, -3260) * mm, "mid": v(5697.72, -2694.31) * mm, "end": v(5132.04, -2460) * mm});
            skLineSegment(sketch, "E101", {"start": v(5132.04, -2460) * mm, "end": v(5132.04, -3260) * mm});
            skArc(sketch, "E102", {"start": v(4902.16, -5739.58) * mm, "mid": v(4213.98, -5709.53) * mm, "end": v(3748.62, -5201.68) * mm});
            skLineSegment(sketch, "E103", {"start": v(4594.34, -4893.86) * mm, "end": v(3748.62, -5201.68) * mm});
            skArc(sketch, "E104", {"start": v(5346.19, -5805.04) * mm, "mid": v(5551.21, -5310.06) * mm, "end": v(6046.19, -5105.04) * mm});
            skArc(sketch, "E105", {"start": v(8050, -5110) * mm, "mid": v(7342.9, -4817.1) * mm, "end": v(7050, -4110) * mm});
            skArc(sketch, "E106", {"start": v(9200, -6705.04) * mm, "mid": v(8965.69, -7270.72) * mm, "end": v(8400, -7505.04) * mm});
            skArc(sketch, "E107", {"start": v(7110, -6705.04) * mm, "mid": v(7344.31, -7270.72) * mm, "end": v(7910, -7505.04) * mm});
            skArc(sketch, "E108", {"start": v(6922.42, -11490.39) * mm, "mid": v(6952.46, -10802.22) * mm, "end": v(7460.32, -10336.85) * mm});
            skLineSegment(sketch, "E109", {"start": v(7768.14, -11182.57) * mm, "end": v(7460.32, -10336.85) * mm});
            skLineSegment(sketch, "E110", {"start": v(8400, -7505.04) * mm, "end": v(8400, -6705.04) * mm});
            skLineSegment(sketch, "E111", {"start": v(7910, -6705.04) * mm, "end": v(7910, -7505.04) * mm});
            skLineSegment(sketch, "E112", {"start": v(7050, -4110) * mm, "end": v(8050, -4110) * mm});
            skLineSegment(sketch, "E113", {"start": v(6046.19, -5105.04) * mm, "end": v(6046.19, -5805.04) * mm});
            skArc(sketch, "E114", {"start": v(9400, -6502.52) * mm, "mid": v(10036.4, -6238.91) * mm, "end": v(10300, -5602.52) * mm});
            skLineSegment(sketch, "E115", {"start": v(9400, -5602.52) * mm, "end": v(10300, -5602.52) * mm});
            skSolve(sketch);
        }
        {
            var Q0;
            {var subQ0=sQuery(id+"F0.wireOp",EDGE,"E27");var subQ1=sQuery(id+"F0.wireOp",EDGE,"E26");var subQ2=sQuery(id+"F0.wireOp",EDGE,"E25");var subQ3=sQuery(id+"F0.wireOp",EDGE,"E21");var subQ4=sQuery(id+"F0.wireOp",EDGE,"E18");var subQ5=sQuery(id+"F0.wireOp",EDGE,"E17");var subQ6=sQuery(id+"F0.wireOp",EDGE,"E16");var subQ7=sQuery(id+"F0.wireOp",EDGE,"E3");var subQ8=sQuery(id+"F0.wireOp",EDGE,"E1");var subQ9=sQuery(id+"F0.wireOp",EDGE,"E0");var subQ10=makeQuery(id+"F1.opExtrude","CAP_FACE",FACE,{"disambiguationData":[OSD([subQ9,subQ8,subQ7,subQ6,subQ5,subQ4,sQuery(id+"F0.wireOp",EDGE,"E19"),sQuery(id+"F0.wireOp",EDGE,"E20"),subQ3,subQ2,subQ1,subQ0])],"isStart":true});Q0=makeQuery(id+"F28.boolean.opBoolean","MERGE",FACE,{"derivedFrom":[makeQuery(id+"F2.boolean.opBoolean","SPLIT",FACE,{"disambiguationData":[TD([makeQuery(id+"F2.opExtrude","SWEPT_FACE",FACE,{"disambiguationData":[OSD([sQuery(id+"F0.wireOp",EDGE,"E8.0")])]})])],"derivedFrom":subQ10}),makeQuery(id+"F26.boolean.opBoolean","MERGE",FACE,{"derivedFrom":[makeQuery(id+"F4.boolean.opBoolean","MERGE",FACE,{"derivedFrom":[makeQuery(id+"F2.boolean.opBoolean","SPLIT",FACE,{"disambiguationData":[TD([makeQuery(id+"F1.opExtrude","SWEPT_FACE",FACE,{"disambiguationData":[OSD([subQ5])]})])],"derivedFrom":subQ10}),makeQuery(id+"F2.boolean.opBoolean","SPLIT",FACE,{"disambiguationData":[TD([makeQuery(id+"F2.opExtrude","SWEPT_FACE",FACE,{"disambiguationData":[OSD([sQuery(id+"F0.wireOp",EDGE,"E4.1")])]})])],"derivedFrom":subQ10}),makeQuery(id+"F4.opExtrude","SWEPT_FACE",FACE,{"disambiguationData":[OSD([sQuery(id+"F3.wireOp",EDGE,"E61.bottom")])]})]}),makeQuery(id+"F24.boolean.opBoolean","MERGE",FACE,{"derivedFrom":[makeQuery(id+"F6.boolean.opBoolean","MERGE",FACE,{"derivedFrom":[makeQuery(id+"F2.boolean.opBoolean","SPLIT",FACE,{"disambiguationData":[TD([makeQuery(id+"F1.opExtrude","SWEPT_FACE",FACE,{"disambiguationData":[OSD([subQ2])]})])],"derivedFrom":subQ10}),makeQuery(id+"F2.boolean.opBoolean","SPLIT",FACE,{"disambiguationData":[TD([makeQuery(id+"F2.opExtrude","SWEPT_FACE",FACE,{"disambiguationData":[OSD([sQuery(id+"F0.wireOp",EDGE,"E4.0")])]})])],"derivedFrom":subQ10}),makeQuery(id+"F6.opExtrude","SWEPT_FACE",FACE,{"disambiguationData":[OSD([sQuery(id+"F5.wireOp",EDGE,"E63.bottom")])]})]}),makeQuery(id+"F22.boolean.opBoolean","MERGE",FACE,{"derivedFrom":[makeQuery(id+"F2.boolean.opBoolean","SPLIT",FACE,{"disambiguationData":[TD([makeQuery(id+"F2.opExtrude","SWEPT_FACE",FACE,{"disambiguationData":[OSD([sQuery(id+"F0.wireOp",EDGE,"E4.3")])]})])],"derivedFrom":subQ10}),makeQuery(id+"F20.boolean.opBoolean","MERGE",FACE,{"derivedFrom":[makeQuery(id+"F18.boolean.opBoolean","MERGE",FACE,{"derivedFrom":[makeQuery(id+"F2.boolean.opBoolean","SPLIT",FACE,{"disambiguationData":[TD([makeQuery(id+"F2.opExtrude","SWEPT_FACE",FACE,{"disambiguationData":[OSD([sQuery(id+"F0.wireOp",EDGE,"E30")])]})])],"derivedFrom":subQ10}),makeQuery(id+"F16.boolean.opBoolean","MERGE",FACE,{"derivedFrom":[makeQuery(id+"F2.boolean.opBoolean","SPLIT",FACE,{"disambiguationData":[TD([makeQuery(id+"F2.opExtrude","SWEPT_FACE",FACE,{"disambiguationData":[OSD([sQuery(id+"F0.wireOp",EDGE,"E8.1")])]})])],"derivedFrom":subQ10}),makeQuery(id+"F14.boolean.opBoolean","MERGE",FACE,{"derivedFrom":[makeQuery(id+"F2.boolean.opBoolean","SPLIT",FACE,{"disambiguationData":[TD([makeQuery(id+"F2.opExtrude","SWEPT_FACE",FACE,{"disambiguationData":[OSD([sQuery(id+"F0.wireOp",EDGE,"E24.0")])]})])],"derivedFrom":subQ10}),makeQuery(id+"F12.boolean.opBoolean","MERGE",FACE,{"derivedFrom":[makeQuery(id+"F2.boolean.opBoolean","SPLIT",FACE,{"disambiguationData":[TD([makeQuery(id+"F2.opExtrude","SWEPT_FACE",FACE,{"disambiguationData":[OSD([sQuery(id+"F0.wireOp",EDGE,"E22.0")])]})])],"derivedFrom":subQ10}),makeQuery(id+"F2.boolean.opBoolean","SPLIT",FACE,{"disambiguationData":[TD([makeQuery(id+"F2.opExtrude","SWEPT_FACE",FACE,{"disambiguationData":[OSD([sQuery(id+"F0.wireOp",EDGE,"E23.0")])]})])],"derivedFrom":subQ10}),makeQuery(id+"F12.opExtrude","SWEPT_FACE",FACE,{"disambiguationData":[OSD([sQuery(id+"F11.wireOp",EDGE,"E69"),sQuery(id+"F11.wireOp",EDGE,"E73")])]})]}),makeQuery(id+"F14.opExtrude","SWEPT_FACE",FACE,{"disambiguationData":[OSD([sQuery(id+"F13.wireOp",EDGE,"E74"),sQuery(id+"F13.wireOp",EDGE,"E78")])]})]}),makeQuery(id+"F16.opExtrude","SWEPT_FACE",FACE,{"disambiguationData":[OSD([sQuery(id+"F15.wireOp",EDGE,"E79.bottom")])]})]}),makeQuery(id+"F18.opExtrude","SWEPT_FACE",FACE,{"disambiguationData":[OSD([sQuery(id+"F17.wireOp",EDGE,"E80"),sQuery(id+"F17.wireOp",EDGE,"E84")])]})]}),makeQuery(id+"F20.opExtrude","SWEPT_FACE",FACE,{"disambiguationData":[OSD([sQuery(id+"F19.wireOp",EDGE,"E85.bottom")])]})]}),makeQuery(id+"F22.opExtrude","SWEPT_FACE",FACE,{"disambiguationData":[OSD([sQuery(id+"F21.wireOp",EDGE,"E86.bottom")])]})]}),makeQuery(id+"F24.opExtrude","SWEPT_FACE",FACE,{"disambiguationData":[OSD([sQuery(id+"F23.wireOp",EDGE,"E88.bottom")])]})]}),makeQuery(id+"F26.opExtrude","SWEPT_FACE",FACE,{"disambiguationData":[OSD([sQuery(id+"F25.wireOp",EDGE,"E89.bottom")])]})]}),makeQuery(id+"F28.opExtrude","SWEPT_FACE",FACE,{"disambiguationData":[OSD([sQuery(id+"F27.wireOp",EDGE,"E90"),sQuery(id+"F27.wireOp",EDGE,"E94")])]})]});}
            var sketch = newSketch(context, id + "F30", { "sketchPlane" : qUnion([Q0])});
            skLineSegment(sketch, "E116", {"start": v(2968.17, -7424.03) * mm, "end": v(4612.63, -6825.5) * mm});
            skLineSegment(sketch, "E117", {"start": v(4612.63, -6825.5) * mm, "end": v(4356.12, -6120.72) * mm});
            skLineSegment(sketch, "E118", {"start": v(4356.12, -6120.72) * mm, "end": v(2711.65, -6719.26) * mm});
            skLineSegment(sketch, "E119", {"start": v(2711.65, -6719.26) * mm, "end": v(2968.17, -7424.03) * mm});
            skSolve(sketch);
        }
        {
            var Q0;
            Q0 = qSketchRegion(id + "F30", true);
            extrude(context, id + "F31", {"entities" : qUnion([Q0]), "depth" : 500 * mm});
        }
        {
            var Q0;
            {var subQ0=sQuery(id+"F0.wireOp",EDGE,"E27");var subQ1=sQuery(id+"F0.wireOp",EDGE,"E26");var subQ2=sQuery(id+"F0.wireOp",EDGE,"E25");var subQ3=sQuery(id+"F0.wireOp",EDGE,"E21");var subQ4=sQuery(id+"F0.wireOp",EDGE,"E18");var subQ5=sQuery(id+"F0.wireOp",EDGE,"E17");var subQ6=sQuery(id+"F0.wireOp",EDGE,"E16");var subQ7=sQuery(id+"F0.wireOp",EDGE,"E3");var subQ8=sQuery(id+"F0.wireOp",EDGE,"E1");var subQ9=sQuery(id+"F0.wireOp",EDGE,"E0");var subQ10=makeQuery(id+"F1.opExtrude","CAP_FACE",FACE,{"disambiguationData":[OSD([subQ9,subQ8,subQ7,subQ6,subQ5,subQ4,sQuery(id+"F0.wireOp",EDGE,"E19"),sQuery(id+"F0.wireOp",EDGE,"E20"),subQ3,subQ2,subQ1,subQ0])],"isStart":true});Q0=makeQuery(id+"F28.boolean.opBoolean","MERGE",FACE,{"derivedFrom":[makeQuery(id+"F2.boolean.opBoolean","SPLIT",FACE,{"disambiguationData":[TD([makeQuery(id+"F2.opExtrude","SWEPT_FACE",FACE,{"disambiguationData":[OSD([sQuery(id+"F0.wireOp",EDGE,"E8.0")])]})])],"derivedFrom":subQ10}),makeQuery(id+"F26.boolean.opBoolean","MERGE",FACE,{"derivedFrom":[makeQuery(id+"F4.boolean.opBoolean","MERGE",FACE,{"derivedFrom":[makeQuery(id+"F2.boolean.opBoolean","SPLIT",FACE,{"disambiguationData":[TD([makeQuery(id+"F1.opExtrude","SWEPT_FACE",FACE,{"disambiguationData":[OSD([subQ5])]})])],"derivedFrom":subQ10}),makeQuery(id+"F2.boolean.opBoolean","SPLIT",FACE,{"disambiguationData":[TD([makeQuery(id+"F2.opExtrude","SWEPT_FACE",FACE,{"disambiguationData":[OSD([sQuery(id+"F0.wireOp",EDGE,"E4.1")])]})])],"derivedFrom":subQ10}),makeQuery(id+"F4.opExtrude","SWEPT_FACE",FACE,{"disambiguationData":[OSD([sQuery(id+"F3.wireOp",EDGE,"E61.bottom")])]})]}),makeQuery(id+"F24.boolean.opBoolean","MERGE",FACE,{"derivedFrom":[makeQuery(id+"F6.boolean.opBoolean","MERGE",FACE,{"derivedFrom":[makeQuery(id+"F2.boolean.opBoolean","SPLIT",FACE,{"disambiguationData":[TD([makeQuery(id+"F1.opExtrude","SWEPT_FACE",FACE,{"disambiguationData":[OSD([subQ2])]})])],"derivedFrom":subQ10}),makeQuery(id+"F2.boolean.opBoolean","SPLIT",FACE,{"disambiguationData":[TD([makeQuery(id+"F2.opExtrude","SWEPT_FACE",FACE,{"disambiguationData":[OSD([sQuery(id+"F0.wireOp",EDGE,"E4.0")])]})])],"derivedFrom":subQ10}),makeQuery(id+"F6.opExtrude","SWEPT_FACE",FACE,{"disambiguationData":[OSD([sQuery(id+"F5.wireOp",EDGE,"E63.bottom")])]})]}),makeQuery(id+"F22.boolean.opBoolean","MERGE",FACE,{"derivedFrom":[makeQuery(id+"F2.boolean.opBoolean","SPLIT",FACE,{"disambiguationData":[TD([makeQuery(id+"F2.opExtrude","SWEPT_FACE",FACE,{"disambiguationData":[OSD([sQuery(id+"F0.wireOp",EDGE,"E4.3")])]})])],"derivedFrom":subQ10}),makeQuery(id+"F20.boolean.opBoolean","MERGE",FACE,{"derivedFrom":[makeQuery(id+"F18.boolean.opBoolean","MERGE",FACE,{"derivedFrom":[makeQuery(id+"F2.boolean.opBoolean","SPLIT",FACE,{"disambiguationData":[TD([makeQuery(id+"F2.opExtrude","SWEPT_FACE",FACE,{"disambiguationData":[OSD([sQuery(id+"F0.wireOp",EDGE,"E30")])]})])],"derivedFrom":subQ10}),makeQuery(id+"F16.boolean.opBoolean","MERGE",FACE,{"derivedFrom":[makeQuery(id+"F2.boolean.opBoolean","SPLIT",FACE,{"disambiguationData":[TD([makeQuery(id+"F2.opExtrude","SWEPT_FACE",FACE,{"disambiguationData":[OSD([sQuery(id+"F0.wireOp",EDGE,"E8.1")])]})])],"derivedFrom":subQ10}),makeQuery(id+"F14.boolean.opBoolean","MERGE",FACE,{"derivedFrom":[makeQuery(id+"F2.boolean.opBoolean","SPLIT",FACE,{"disambiguationData":[TD([makeQuery(id+"F2.opExtrude","SWEPT_FACE",FACE,{"disambiguationData":[OSD([sQuery(id+"F0.wireOp",EDGE,"E24.0")])]})])],"derivedFrom":subQ10}),makeQuery(id+"F12.boolean.opBoolean","MERGE",FACE,{"derivedFrom":[makeQuery(id+"F2.boolean.opBoolean","SPLIT",FACE,{"disambiguationData":[TD([makeQuery(id+"F2.opExtrude","SWEPT_FACE",FACE,{"disambiguationData":[OSD([sQuery(id+"F0.wireOp",EDGE,"E22.0")])]})])],"derivedFrom":subQ10}),makeQuery(id+"F2.boolean.opBoolean","SPLIT",FACE,{"disambiguationData":[TD([makeQuery(id+"F2.opExtrude","SWEPT_FACE",FACE,{"disambiguationData":[OSD([sQuery(id+"F0.wireOp",EDGE,"E23.0")])]})])],"derivedFrom":subQ10}),makeQuery(id+"F12.opExtrude","SWEPT_FACE",FACE,{"disambiguationData":[OSD([sQuery(id+"F11.wireOp",EDGE,"E69"),sQuery(id+"F11.wireOp",EDGE,"E73")])]})]}),makeQuery(id+"F14.opExtrude","SWEPT_FACE",FACE,{"disambiguationData":[OSD([sQuery(id+"F13.wireOp",EDGE,"E74"),sQuery(id+"F13.wireOp",EDGE,"E78")])]})]}),makeQuery(id+"F16.opExtrude","SWEPT_FACE",FACE,{"disambiguationData":[OSD([sQuery(id+"F15.wireOp",EDGE,"E79.bottom")])]})]}),makeQuery(id+"F18.opExtrude","SWEPT_FACE",FACE,{"disambiguationData":[OSD([sQuery(id+"F17.wireOp",EDGE,"E80"),sQuery(id+"F17.wireOp",EDGE,"E84")])]})]}),makeQuery(id+"F20.opExtrude","SWEPT_FACE",FACE,{"disambiguationData":[OSD([sQuery(id+"F19.wireOp",EDGE,"E85.bottom")])]})]}),makeQuery(id+"F22.opExtrude","SWEPT_FACE",FACE,{"disambiguationData":[OSD([sQuery(id+"F21.wireOp",EDGE,"E86.bottom")])]})]}),makeQuery(id+"F24.opExtrude","SWEPT_FACE",FACE,{"disambiguationData":[OSD([sQuery(id+"F23.wireOp",EDGE,"E88.bottom")])]})]}),makeQuery(id+"F26.opExtrude","SWEPT_FACE",FACE,{"disambiguationData":[OSD([sQuery(id+"F25.wireOp",EDGE,"E89.bottom")])]})]}),makeQuery(id+"F28.opExtrude","SWEPT_FACE",FACE,{"disambiguationData":[OSD([sQuery(id+"F27.wireOp",EDGE,"E90"),sQuery(id+"F27.wireOp",EDGE,"E94")])]})]});}
            var sketch = newSketch(context, id + "F32", { "sketchPlane" : qUnion([Q0])});
            skLineSegment(sketch, "E120", {"start": v(5217.3, -6605.41) * mm, "end": v(4653.48, -6810.63) * mm});
            skLineSegment(sketch, "E121", {"start": v(4653.48, -6810.63) * mm, "end": v(4448.27, -6246.81) * mm});
            skLineSegment(sketch, "E122", {"start": v(4448.27, -6246.81) * mm, "end": v(5012.08, -6041.6) * mm});
            skLineSegment(sketch, "E123", {"start": v(5012.08, -6041.6) * mm, "end": v(5217.3, -6605.41) * mm});
            skSolve(sketch);
        }
        {
            var Q0;
            Q0 = qSketchRegion(id + "F32", true);
            extrude(context, id + "F33", {"entities" : qUnion([Q0]), "depth" : 800 * mm});
        }
        {
            var Q0;
            {var subQ0=sQuery(id+"F0.wireOp",EDGE,"E27");var subQ1=sQuery(id+"F0.wireOp",EDGE,"E26");var subQ2=sQuery(id+"F0.wireOp",EDGE,"E25");var subQ3=sQuery(id+"F0.wireOp",EDGE,"E21");var subQ4=sQuery(id+"F0.wireOp",EDGE,"E18");var subQ5=sQuery(id+"F0.wireOp",EDGE,"E17");var subQ6=sQuery(id+"F0.wireOp",EDGE,"E16");var subQ7=sQuery(id+"F0.wireOp",EDGE,"E3");var subQ8=sQuery(id+"F0.wireOp",EDGE,"E1");var subQ9=sQuery(id+"F0.wireOp",EDGE,"E0");var subQ10=makeQuery(id+"F1.opExtrude","CAP_FACE",FACE,{"disambiguationData":[OSD([subQ9,subQ8,subQ7,subQ6,subQ5,subQ4,sQuery(id+"F0.wireOp",EDGE,"E19"),sQuery(id+"F0.wireOp",EDGE,"E20"),subQ3,subQ2,subQ1,subQ0])],"isStart":true});Q0=makeQuery(id+"F28.boolean.opBoolean","MERGE",FACE,{"derivedFrom":[makeQuery(id+"F2.boolean.opBoolean","SPLIT",FACE,{"disambiguationData":[TD([makeQuery(id+"F2.opExtrude","SWEPT_FACE",FACE,{"disambiguationData":[OSD([sQuery(id+"F0.wireOp",EDGE,"E8.0")])]})])],"derivedFrom":subQ10}),makeQuery(id+"F26.boolean.opBoolean","MERGE",FACE,{"derivedFrom":[makeQuery(id+"F4.boolean.opBoolean","MERGE",FACE,{"derivedFrom":[makeQuery(id+"F2.boolean.opBoolean","SPLIT",FACE,{"disambiguationData":[TD([makeQuery(id+"F1.opExtrude","SWEPT_FACE",FACE,{"disambiguationData":[OSD([subQ5])]})])],"derivedFrom":subQ10}),makeQuery(id+"F2.boolean.opBoolean","SPLIT",FACE,{"disambiguationData":[TD([makeQuery(id+"F2.opExtrude","SWEPT_FACE",FACE,{"disambiguationData":[OSD([sQuery(id+"F0.wireOp",EDGE,"E4.1")])]})])],"derivedFrom":subQ10}),makeQuery(id+"F4.opExtrude","SWEPT_FACE",FACE,{"disambiguationData":[OSD([sQuery(id+"F3.wireOp",EDGE,"E61.bottom")])]})]}),makeQuery(id+"F24.boolean.opBoolean","MERGE",FACE,{"derivedFrom":[makeQuery(id+"F6.boolean.opBoolean","MERGE",FACE,{"derivedFrom":[makeQuery(id+"F2.boolean.opBoolean","SPLIT",FACE,{"disambiguationData":[TD([makeQuery(id+"F1.opExtrude","SWEPT_FACE",FACE,{"disambiguationData":[OSD([subQ2])]})])],"derivedFrom":subQ10}),makeQuery(id+"F2.boolean.opBoolean","SPLIT",FACE,{"disambiguationData":[TD([makeQuery(id+"F2.opExtrude","SWEPT_FACE",FACE,{"disambiguationData":[OSD([sQuery(id+"F0.wireOp",EDGE,"E4.0")])]})])],"derivedFrom":subQ10}),makeQuery(id+"F6.opExtrude","SWEPT_FACE",FACE,{"disambiguationData":[OSD([sQuery(id+"F5.wireOp",EDGE,"E63.bottom")])]})]}),makeQuery(id+"F22.boolean.opBoolean","MERGE",FACE,{"derivedFrom":[makeQuery(id+"F2.boolean.opBoolean","SPLIT",FACE,{"disambiguationData":[TD([makeQuery(id+"F2.opExtrude","SWEPT_FACE",FACE,{"disambiguationData":[OSD([sQuery(id+"F0.wireOp",EDGE,"E4.3")])]})])],"derivedFrom":subQ10}),makeQuery(id+"F20.boolean.opBoolean","MERGE",FACE,{"derivedFrom":[makeQuery(id+"F18.boolean.opBoolean","MERGE",FACE,{"derivedFrom":[makeQuery(id+"F2.boolean.opBoolean","SPLIT",FACE,{"disambiguationData":[TD([makeQuery(id+"F2.opExtrude","SWEPT_FACE",FACE,{"disambiguationData":[OSD([sQuery(id+"F0.wireOp",EDGE,"E30")])]})])],"derivedFrom":subQ10}),makeQuery(id+"F16.boolean.opBoolean","MERGE",FACE,{"derivedFrom":[makeQuery(id+"F2.boolean.opBoolean","SPLIT",FACE,{"disambiguationData":[TD([makeQuery(id+"F2.opExtrude","SWEPT_FACE",FACE,{"disambiguationData":[OSD([sQuery(id+"F0.wireOp",EDGE,"E8.1")])]})])],"derivedFrom":subQ10}),makeQuery(id+"F14.boolean.opBoolean","MERGE",FACE,{"derivedFrom":[makeQuery(id+"F2.boolean.opBoolean","SPLIT",FACE,{"disambiguationData":[TD([makeQuery(id+"F2.opExtrude","SWEPT_FACE",FACE,{"disambiguationData":[OSD([sQuery(id+"F0.wireOp",EDGE,"E24.0")])]})])],"derivedFrom":subQ10}),makeQuery(id+"F12.boolean.opBoolean","MERGE",FACE,{"derivedFrom":[makeQuery(id+"F2.boolean.opBoolean","SPLIT",FACE,{"disambiguationData":[TD([makeQuery(id+"F2.opExtrude","SWEPT_FACE",FACE,{"disambiguationData":[OSD([sQuery(id+"F0.wireOp",EDGE,"E22.0")])]})])],"derivedFrom":subQ10}),makeQuery(id+"F2.boolean.opBoolean","SPLIT",FACE,{"disambiguationData":[TD([makeQuery(id+"F2.opExtrude","SWEPT_FACE",FACE,{"disambiguationData":[OSD([sQuery(id+"F0.wireOp",EDGE,"E23.0")])]})])],"derivedFrom":subQ10}),makeQuery(id+"F12.opExtrude","SWEPT_FACE",FACE,{"disambiguationData":[OSD([sQuery(id+"F11.wireOp",EDGE,"E69"),sQuery(id+"F11.wireOp",EDGE,"E73")])]})]}),makeQuery(id+"F14.opExtrude","SWEPT_FACE",FACE,{"disambiguationData":[OSD([sQuery(id+"F13.wireOp",EDGE,"E74"),sQuery(id+"F13.wireOp",EDGE,"E78")])]})]}),makeQuery(id+"F16.opExtrude","SWEPT_FACE",FACE,{"disambiguationData":[OSD([sQuery(id+"F15.wireOp",EDGE,"E79.bottom")])]})]}),makeQuery(id+"F18.opExtrude","SWEPT_FACE",FACE,{"disambiguationData":[OSD([sQuery(id+"F17.wireOp",EDGE,"E80"),sQuery(id+"F17.wireOp",EDGE,"E84")])]})]}),makeQuery(id+"F20.opExtrude","SWEPT_FACE",FACE,{"disambiguationData":[OSD([sQuery(id+"F19.wireOp",EDGE,"E85.bottom")])]})]}),makeQuery(id+"F22.opExtrude","SWEPT_FACE",FACE,{"disambiguationData":[OSD([sQuery(id+"F21.wireOp",EDGE,"E86.bottom")])]})]}),makeQuery(id+"F24.opExtrude","SWEPT_FACE",FACE,{"disambiguationData":[OSD([sQuery(id+"F23.wireOp",EDGE,"E88.bottom")])]})]}),makeQuery(id+"F26.opExtrude","SWEPT_FACE",FACE,{"disambiguationData":[OSD([sQuery(id+"F25.wireOp",EDGE,"E89.bottom")])]})]}),makeQuery(id+"F28.opExtrude","SWEPT_FACE",FACE,{"disambiguationData":[OSD([sQuery(id+"F27.wireOp",EDGE,"E90"),sQuery(id+"F27.wireOp",EDGE,"E94")])]})]});}
            var sketch = newSketch(context, id + "F34", { "sketchPlane" : qUnion([Q0])});
            skLineSegment(sketch, "E124", {"start": v(2498.54, -5446.87) * mm, "end": v(2498.54, -5126.87) * mm});
            skLineSegment(sketch, "E125", {"start": v(2498.54, -5126.87) * mm, "end": v(2978.54, -5126.87) * mm});
            skLineSegment(sketch, "E126", {"start": v(2978.54, -5126.87) * mm, "end": v(2978.54, -5766.87) * mm});
            skLineSegment(sketch, "E127", {"start": v(2978.54, -5766.87) * mm, "end": v(2498.54, -5766.87) * mm});
            skLineSegment(sketch, "E128", {"start": v(2498.54, -5766.87) * mm, "end": v(2498.54, -5446.87) * mm});
            skSolve(sketch);
        }
        {
            var Q0;
            Q0 = qSketchRegion(id + "F34", true);
            extrude(context, id + "F35", {"entities" : qUnion([Q0]), "depth" : 900 * mm});
        }
        {
            var Q0;
            Q0=makeQuery(id+"F29.imprint","IMPRINT",FACE,{"disambiguationData":[TD([[makeQuery(id+"F29.imprint","IMPRINT",EDGE,{"derivedFrom":sQuery(id+"F29.wireOp",EDGE,"E98")}),1.0]])]});
            var sketch = newSketch(context, id + "F36", { "sketchPlane" : qUnion([Q0])});
            skPoint(sketch, "E129.0", {"position": v(8050, -3510) * mm});
            skLineSegment(sketch, "E130.bottom", {"start": v(8050, -3510) * mm, "end": v(7630, -3510) * mm});
            skLineSegment(sketch, "E130.top", {"start": v(8050, -4070) * mm, "end": v(7630, -4070) * mm});
            skLineSegment(sketch, "E130.left", {"start": v(8050, -3510) * mm, "end": v(8050, -4070) * mm});
            skLineSegment(sketch, "E130.right", {"start": v(7630, -3510) * mm, "end": v(7630, -4070) * mm});
            skSolve(sketch);
        }
        {
            var Q0;
            Q0 = qSketchRegion(id + "F36", true);
            var Q1;
            Q1=makeQuery(id+"F2.opExtrude","CAP_FACE",FACE,{"disambiguationData":[OSD([sQuery(id+"F0.wireOp",EDGE,"E0"),sQuery(id+"F0.wireOp",EDGE,"E1"),sQuery(id+"F0.wireOp",EDGE,"E2"),sQuery(id+"F0.wireOp",EDGE,"E3"),sQuery(id+"F0.wireOp",EDGE,"E4.0"),sQuery(id+"F0.wireOp",EDGE,"E4.1"),sQuery(id+"F0.wireOp",EDGE,"E4.2"),sQuery(id+"F0.wireOp",EDGE,"E4.3"),sQuery(id+"F0.wireOp",EDGE,"E5"),sQuery(id+"F0.wireOp",EDGE,"E6"),sQuery(id+"F0.wireOp",EDGE,"E7"),sQuery(id+"F0.wireOp",EDGE,"E8.0"),sQuery(id+"F0.wireOp",EDGE,"E8.1"),sQuery(id+"F0.wireOp",EDGE,"E8.2"),sQuery(id+"F0.wireOp",EDGE,"E9"),sQuery(id+"F0.wireOp",EDGE,"E10.0"),sQuery(id+"F0.wireOp",EDGE,"E11"),sQuery(id+"F0.wireOp",EDGE,"E12"),sQuery(id+"F0.wireOp",EDGE,"E13.0"),sQuery(id+"F0.wireOp",EDGE,"E13.1"),sQuery(id+"F0.wireOp",EDGE,"E14"),sQuery(id+"F0.wireOp",EDGE,"E15.0"),sQuery(id+"F0.wireOp",EDGE,"E19"),sQuery(id+"F0.wireOp",EDGE,"E20"),sQuery(id+"F0.wireOp",EDGE,"E21"),sQuery(id+"F0.wireOp",EDGE,"E22.0"),sQuery(id+"F0.wireOp",EDGE,"E23.0"),sQuery(id+"F0.wireOp",EDGE,"E24.0"),sQuery(id+"F0.wireOp",EDGE,"E28"),sQuery(id+"F0.wireOp",EDGE,"E29.0"),sQuery(id+"F0.wireOp",EDGE,"E30"),sQuery(id+"F0.wireOp",EDGE,"E31"),sQuery(id+"F0.wireOp",EDGE,"E32.0"),sQuery(id+"F0.wireOp",EDGE,"E32.1"),sQuery(id+"F0.wireOp",EDGE,"E33"),sQuery(id+"F0.wireOp",EDGE,"E34.0"),sQuery(id+"F0.wireOp",EDGE,"E35"),sQuery(id+"F0.wireOp",EDGE,"E36"),sQuery(id+"F0.wireOp",EDGE,"E37"),sQuery(id+"F0.wireOp",EDGE,"E38.0"),sQuery(id+"F0.wireOp",EDGE,"E38.1"),sQuery(id+"F0.wireOp",EDGE,"E38.2"),sQuery(id+"F0.wireOp",EDGE,"E39"),sQuery(id+"F0.wireOp",EDGE,"E40"),sQuery(id+"F0.wireOp",EDGE,"E41.0"),sQuery(id+"F0.wireOp",EDGE,"E41.1"),sQuery(id+"F0.wireOp",EDGE,"E42.trimOffspring"),sQuery(id+"F0.wireOp",EDGE,"E43.trimOffspring"),sQuery(id+"F0.wireOp",EDGE,"E44.trimOffspring"),sQuery(id+"F0.wireOp",EDGE,"E45.trimOffspring"),sQuery(id+"F0.wireOp",EDGE,"E46.trimOffspring"),sQuery(id+"F0.wireOp",EDGE,"E47.trimOffspring"),sQuery(id+"F0.wireOp",EDGE,"E48.trimOffspring"),sQuery(id+"F0.wireOp",EDGE,"E49.trimOffspring"),sQuery(id+"F0.wireOp",EDGE,"E50.trimOffspring"),sQuery(id+"F0.wireOp",EDGE,"E51.trimOffspring"),sQuery(id+"F0.wireOp",EDGE,"E52.trimOffspring"),sQuery(id+"F0.wireOp",EDGE,"E53.trimOffspring"),sQuery(id+"F0.wireOp",EDGE,"E54.trimOffspring"),sQuery(id+"F0.wireOp",EDGE,"E55.trimOffspring"),sQuery(id+"F0.wireOp",EDGE,"E56.trimOffspring"),sQuery(id+"F0.wireOp",EDGE,"E57.trimOffspring"),sQuery(id+"F0.wireOp",EDGE,"E58.trimOffspring"),sQuery(id+"F0.wireOp",EDGE,"E59.trimOffspring"),sQuery(id+"F0.wireOp",EDGE,"E60.trimOffspring")])],"isStart":false});
            extrude(context, id + "F37", {"entities" : qUnion([Q0]), "operationType" : NewBodyOperationType.ADD, "endBound" : BoundingType.UP_TO_SURFACE, "endBoundEntityFace" : qUnion([Q1]), "depth" : 25 * mm});
        }
        {
            var Q0;
            Q0=makeQuery(id+"F2.opExtrude","SWEPT_FACE",FACE,{"disambiguationData":[OSD([sQuery(id+"F0.wireOp",EDGE,"E13.1")])]});
            var sketch = newSketch(context, id + "F38", { "sketchPlane" : qUnion([Q0])});
            skLineSegment(sketch, "E131.bottom", {"start": v(-2493.47, 1079.92) * mm, "end": v(-1893.47, 1079.92) * mm});
            skLineSegment(sketch, "E131.top", {"start": v(-2493.47, 2079.92) * mm, "end": v(-1893.47, 2079.92) * mm});
            skLineSegment(sketch, "E131.left", {"start": v(-2493.47, 1079.92) * mm, "end": v(-2493.47, 2079.92) * mm});
            skLineSegment(sketch, "E131.right", {"start": v(-1893.47, 1079.92) * mm, "end": v(-1893.47, 2079.92) * mm});
            skSolve(sketch);
        }
        {
            var Q0;
            Q0 = qSketchRegion(id + "F38", true);
            extrude(context, id + "F39", {"entities" : qUnion([Q0]), "depth" : 600 * mm});
        }
        {
            var Q0;
            Q0=makeQuery(id+"F29.imprint","IMPRINT",FACE,{"disambiguationData":[TD([[makeQuery(id+"F29.imprint","IMPRINT",EDGE,{"derivedFrom":sQuery(id+"F29.wireOp",EDGE,"E96")}),-1.0]])]});
            var sketch = newSketch(context, id + "F40", { "sketchPlane" : qUnion([Q0])});
            skLineSegment(sketch, "E132.bottom", {"start": v(9221.91, -2832.39) * mm, "end": v(10791.91, -2832.39) * mm});
            skLineSegment(sketch, "E132.top", {"start": v(9221.91, -4932.39) * mm, "end": v(10791.91, -4932.39) * mm});
            skLineSegment(sketch, "E132.left", {"start": v(9221.91, -2832.39) * mm, "end": v(9221.91, -4932.39) * mm});
            skLineSegment(sketch, "E132.right", {"start": v(10791.91, -2832.39) * mm, "end": v(10791.91, -4932.39) * mm});
            skSolve(sketch);
        }
        {
            var Q0;
            Q0 = qSketchRegion(id + "F40", true);
            extrude(context, id + "F41", {"entities" : qUnion([Q0]), "depth" : 300 * mm});
        }
        {
            var Q0;
            Q0=makeQuery(id+"F29.imprint","IMPRINT",FACE,{"disambiguationData":[TD([[makeQuery(id+"F29.imprint","IMPRINT",EDGE,{"derivedFrom":sQuery(id+"F29.wireOp",EDGE,"E96")}),-1.0]])]});
            var sketch = newSketch(context, id + "F42", { "sketchPlane" : qUnion([Q0])});
            skLineSegment(sketch, "E133.bottom", {"start": v(-440.94, -1051.26) * mm, "end": v(209.06, -1051.26) * mm});
            skLineSegment(sketch, "E133.top", {"start": v(-440.94, -3051.26) * mm, "end": v(209.06, -3051.26) * mm});
            skLineSegment(sketch, "E133.left", {"start": v(-440.94, -1051.26) * mm, "end": v(-440.94, -3051.26) * mm});
            skLineSegment(sketch, "E133.right", {"start": v(209.06, -1051.26) * mm, "end": v(209.06, -3051.26) * mm});
            skSolve(sketch);
        }
        {
            var Q0;
            Q0 = qSketchRegion(id + "F42", true);
            extrude(context, id + "F43", {"entities" : qUnion([Q0]), "depth" : 2370 * mm});
        }
        {
            var Q0;
            Q0=makeQuery(id+"F29.imprint","IMPRINT",FACE,{"disambiguationData":[TD([[makeQuery(id+"F29.imprint","IMPRINT",EDGE,{"derivedFrom":sQuery(id+"F29.wireOp",EDGE,"E100")}),-1.0]])]});
            var sketch = newSketch(context, id + "F44", { "sketchPlane" : qUnion([Q0])});
            skLineSegment(sketch, "E134.bottom", {"start": v(8837.01, -396.86) * mm, "end": v(10937.01, -396.86) * mm});
            skLineSegment(sketch, "E134.top", {"start": v(8837.01, -2346.86) * mm, "end": v(10937.01, -2346.86) * mm});
            skLineSegment(sketch, "E134.left", {"start": v(8837.01, -396.86) * mm, "end": v(8837.01, -2346.86) * mm});
            skLineSegment(sketch, "E134.right", {"start": v(10937.01, -396.86) * mm, "end": v(10937.01, -2346.86) * mm});
            skSolve(sketch);
        }
        {
            var Q0;
            Q0 = qSketchRegion(id + "F44", true);
            extrude(context, id + "F45", {"entities" : qUnion([Q0]), "depth" : 450 * mm});
        }
        {
            var Q0;
            Q0=makeQuery(id+"F29.imprint","IMPRINT",FACE,{"disambiguationData":[TD([[makeQuery(id+"F29.imprint","IMPRINT",EDGE,{"derivedFrom":sQuery(id+"F29.wireOp",EDGE,"E107")}),-1.0]])]});
            var sketch = newSketch(context, id + "F46", { "sketchPlane" : qUnion([Q0])});
            skLineSegment(sketch, "E135.bottom", {"start": v(-653.61, -5886.85) * mm, "end": v(1596.39, -5886.85) * mm});
            skLineSegment(sketch, "E135.top", {"start": v(-653.61, -6836.85) * mm, "end": v(1596.39, -6836.85) * mm});
            skLineSegment(sketch, "E135.left", {"start": v(-653.61, -5886.85) * mm, "end": v(-653.61, -6836.85) * mm});
            skLineSegment(sketch, "E135.right", {"start": v(1596.39, -5886.85) * mm, "end": v(1596.39, -6836.85) * mm});
            skLineSegment(sketch, "E136.bottom", {"start": v(228.7, -12785.05) * mm, "end": v(2478.7, -12785.05) * mm});
            skLineSegment(sketch, "E136.top", {"start": v(228.7, -13735.05) * mm, "end": v(2478.7, -13735.05) * mm});
            skLineSegment(sketch, "E136.left", {"start": v(228.7, -12785.05) * mm, "end": v(228.7, -13735.05) * mm});
            skLineSegment(sketch, "E136.right", {"start": v(2478.7, -12785.05) * mm, "end": v(2478.7, -13735.05) * mm});
            skSolve(sketch);
        }
        {
            var Q0;
            Q0 = qSketchRegion(id + "F46", true);
            extrude(context, id + "F47", {"entities" : qUnion([Q0]), "depth" : 850 * mm});
        }
        {
            var Q0;
            Q0=makeQuery(id+"F29.imprint","IMPRINT",FACE,{"disambiguationData":[TD([[makeQuery(id+"F29.imprint","IMPRINT",EDGE,{"derivedFrom":sQuery(id+"F29.wireOp",EDGE,"E107")}),-1.0]])]});
            var sketch = newSketch(context, id + "F48", { "sketchPlane" : qUnion([Q0])});
            skLineSegment(sketch, "E137.bottom", {"start": v(-464.84, -9586.7) * mm, "end": v(635.16, -9586.7) * mm});
            skLineSegment(sketch, "E137.top", {"start": v(-464.84, -10286.7) * mm, "end": v(635.16, -10286.7) * mm});
            skLineSegment(sketch, "E137.left", {"start": v(-464.84, -9586.7) * mm, "end": v(-464.84, -10286.7) * mm});
            skLineSegment(sketch, "E137.right", {"start": v(635.16, -9586.7) * mm, "end": v(635.16, -10286.7) * mm});
            skSolve(sketch);
        }
        {
            var Q0;
            Q0 = qSketchRegion(id + "F48", true);
            extrude(context, id + "F49", {"entities" : qUnion([Q0]), "depth" : 520 * mm});
        }
        {
            var Q0;
            Q0=makeQuery(id+"F29.imprint","IMPRINT",FACE,{"disambiguationData":[TD([[makeQuery(id+"F29.imprint","IMPRINT",EDGE,{"derivedFrom":sQuery(id+"F29.wireOp",EDGE,"E107")}),-1.0]])]});
            var sketch = newSketch(context, id + "F50", { "sketchPlane" : qUnion([Q0])});
            skLineSegment(sketch, "E138.bottom", {"start": v(228.75, -7656.03) * mm, "end": v(-221.25, -7656.03) * mm});
            skLineSegment(sketch, "E138.top", {"start": v(228.75, -9056.03) * mm, "end": v(-221.25, -9056.03) * mm});
            skLineSegment(sketch, "E138.left", {"start": v(228.75, -7656.03) * mm, "end": v(228.75, -9056.03) * mm});
            skLineSegment(sketch, "E138.right", {"start": v(-221.25, -7656.03) * mm, "end": v(-221.25, -9056.03) * mm});
            skSolve(sketch);
        }
        {
            var Q0;
            Q0 = qSketchRegion(id + "F50", true);
            extrude(context, id + "F51", {"entities" : qUnion([Q0]), "depth" : 600 * mm});
        }
        {
            var Q0;
            Q0=makeQuery(id+"F29.imprint","IMPRINT",FACE,{"disambiguationData":[TD([[makeQuery(id+"F29.imprint","IMPRINT",EDGE,{"derivedFrom":sQuery(id+"F29.wireOp",EDGE,"E107")}),-1.0]])]});
            var sketch = newSketch(context, id + "F52", { "sketchPlane" : qUnion([Q0])});
            skLineSegment(sketch, "E139.bottom", {"start": v(-554.3, -4091.71) * mm, "end": v(1275.7, -4091.71) * mm});
            skLineSegment(sketch, "E139.top", {"start": v(-554.3, -4541.71) * mm, "end": v(1275.7, -4541.71) * mm});
            skLineSegment(sketch, "E139.left", {"start": v(-554.3, -4091.71) * mm, "end": v(-554.3, -4541.71) * mm});
            skLineSegment(sketch, "E139.right", {"start": v(1275.7, -4091.71) * mm, "end": v(1275.7, -4541.71) * mm});
            skSolve(sketch);
        }
        {
            var Q0;
            Q0 = qSketchRegion(id + "F52", true);
            extrude(context, id + "F53", {"entities" : qUnion([Q0]), "depth" : 860 * mm});
        }
        {
            var Q0;
            Q0=makeQuery(id+"F29.imprint","IMPRINT",FACE,{"disambiguationData":[TD([[makeQuery(id+"F29.imprint","IMPRINT",EDGE,{"derivedFrom":sQuery(id+"F29.wireOp",EDGE,"E106")}),1.0]])]});
            var sketch = newSketch(context, id + "F54", { "sketchPlane" : qUnion([Q0])});
            skLineSegment(sketch, "E140.bottom", {"start": v(2107.9, -7662.86) * mm, "end": v(1207.9, -7662.86) * mm});
            skLineSegment(sketch, "E140.top", {"start": v(2107.9, -9462.86) * mm, "end": v(1207.9, -9462.86) * mm});
            skLineSegment(sketch, "E140.left", {"start": v(2107.9, -7662.86) * mm, "end": v(2107.9, -9462.86) * mm});
            skLineSegment(sketch, "E140.right", {"start": v(1207.9, -7662.86) * mm, "end": v(1207.9, -9462.86) * mm});
            skSolve(sketch);
        }
        {
            var Q0;
            Q0 = qSketchRegion(id + "F54", true);
            extrude(context, id + "F55", {"entities" : qUnion([Q0]), "depth" : 750 * mm});
        }
        {
            var Q0;
            Q0=makeQuery(id+"F46.imprint","IMPRINT",FACE,{"disambiguationData":[TD([[makeQuery(id+"F46.imprint","IMPRINT",EDGE,{"derivedFrom":sQuery(id+"F46.wireOp",EDGE,"E136.bottom")}),-1.0]])]});
            extrude(context, id + "F56", {"entities" : qUnion([Q0]), "depth" : 850 * mm});
        }
        {
            var Q0;
            Q0=makeQuery(id+"F29.imprint","IMPRINT",FACE,{"disambiguationData":[TD([[makeQuery(id+"F29.imprint","IMPRINT",EDGE,{"derivedFrom":sQuery(id+"F29.wireOp",EDGE,"E107")}),-1.0]])]});
            var sketch = newSketch(context, id + "F57", { "sketchPlane" : qUnion([Q0])});
            skLineSegment(sketch, "E141.bottom", {"start": v(-131.29, -12202.12) * mm, "end": v(2868.71, -12202.12) * mm});
            skLineSegment(sketch, "E141.top", {"start": v(-131.29, -11602.12) * mm, "end": v(2868.71, -11602.12) * mm});
            skLineSegment(sketch, "E141.left", {"start": v(-131.29, -12202.12) * mm, "end": v(-131.29, -11602.12) * mm});
            skLineSegment(sketch, "E141.right", {"start": v(2868.71, -12202.12) * mm, "end": v(2868.71, -11602.12) * mm});
            skSolve(sketch);
        }
        {
            var Q0;
            Q0=makeQuery(id+"F57.imprint","IMPRINT",FACE,{"disambiguationData":[TD([[makeQuery(id+"F57.imprint","IMPRINT",EDGE,{"derivedFrom":sQuery(id+"F57.wireOp",EDGE,"E141.bottom")}),1.0]])]});
            extrude(context, id + "F58", {"entities" : qUnion([Q0]), "depth" : 900 * mm});
        }
        {
            var Q0;
            Q0=makeQuery(id+"F29.imprint","IMPRINT",FACE,{"disambiguationData":[TD([[makeQuery(id+"F29.imprint","IMPRINT",EDGE,{"derivedFrom":sQuery(id+"F29.wireOp",EDGE,"E107")}),-1.0]])]});
            var sketch = newSketch(context, id + "F59", { "sketchPlane" : qUnion([Q0])});
            skLineSegment(sketch, "E142.bottom", {"start": v(12919.18, -11990.89) * mm, "end": v(12319.18, -11990.89) * mm});
            skLineSegment(sketch, "E142.top", {"start": v(12919.18, -8990.89) * mm, "end": v(12319.18, -8990.89) * mm});
            skLineSegment(sketch, "E142.left", {"start": v(12919.18, -11990.89) * mm, "end": v(12919.18, -8990.89) * mm});
            skLineSegment(sketch, "E142.right", {"start": v(12319.18, -11990.89) * mm, "end": v(12319.18, -8990.89) * mm});
            skSolve(sketch);
        }
        {
            var Q0;
            Q0 = qSketchRegion(id + "F59", true);
            extrude(context, id + "F60", {"entities" : qUnion([Q0]), "depth" : 2500 * mm});
        }
        {
            var Q0;
            Q0=makeQuery(id+"F29.imprint","IMPRINT",FACE,{"disambiguationData":[TD([[makeQuery(id+"F29.imprint","IMPRINT",EDGE,{"derivedFrom":sQuery(id+"F29.wireOp",EDGE,"E106")}),1.0]])]});
            var sketch = newSketch(context, id + "F61", { "sketchPlane" : qUnion([Q0])});
            skLineSegment(sketch, "E143.bottom", {"start": v(12818.6, -5304.37) * mm, "end": v(13368.6, -5304.37) * mm});
            skLineSegment(sketch, "E143.top", {"start": v(12818.6, -5664.37) * mm, "end": v(13368.6, -5664.37) * mm});
            skLineSegment(sketch, "E143.left", {"start": v(12818.6, -5304.37) * mm, "end": v(12818.6, -5664.37) * mm});
            skLineSegment(sketch, "E143.right", {"start": v(13368.6, -5304.37) * mm, "end": v(13368.6, -5664.37) * mm});
            skSolve(sketch);
        }
        {
            var Q0;
            Q0 = qSketchRegion(id + "F61", true);
            extrude(context, id + "F62", {"entities" : qUnion([Q0]), "depth" : 400 * mm});
        }
        {
            var Q0;
            Q0=makeQuery(id+"F62.opExtrude","SWEPT_EDGE",EDGE,{"disambiguationData":[OSD([sQuery(id+"F61.wireOp",EDGE,"E143.top"),sQuery(id+"F61.wireOp",EDGE,"E143.left")])]});
            var Q1;
            Q1=makeQuery(id+"F62.opExtrude","SWEPT_EDGE",EDGE,{"disambiguationData":[OSD([sQuery(id+"F61.wireOp",EDGE,"E143.bottom"),sQuery(id+"F61.wireOp",EDGE,"E143.left")])]});
            fillet(context, id + "F63", {"entities" : qUnion([Q0, Q1]), "radius" : 80 * mm, "tangentPropagation" : true, "allowEdgeOverflow" : false});
        }
        {
            var Q0;
            Q0=qCreatedBy(makeId("Top.planeOp"), FACE);
            var sketch = newSketch(context, id + "F64", { "sketchPlane" : qUnion([Q0])});
            skLineSegment(sketch, "E144.bottom", {"start": v(14.21, -15339) * mm, "end": v(1214.21, -15339) * mm});
            skLineSegment(sketch, "E144.top", {"start": v(14.21, -14539) * mm, "end": v(1214.21, -14539) * mm});
            skLineSegment(sketch, "E144.left", {"start": v(14.21, -15339) * mm, "end": v(14.21, -14539) * mm});
            skLineSegment(sketch, "E144.right", {"start": v(1214.21, -15339) * mm, "end": v(1214.21, -14539) * mm});
            skSolve(sketch);
        }
        {
            var Q0;
            Q0 = qSketchRegion(id + "F64", true);
            extrude(context, id + "F65", {"entities" : qUnion([Q0]), "domain" : OperationDomain.MODEL, "flatOperationType" : FlatOperationType.REMOVE, "depth" : 800 * mm, "offsetDistance" : 25 * mm});
        }
    });
